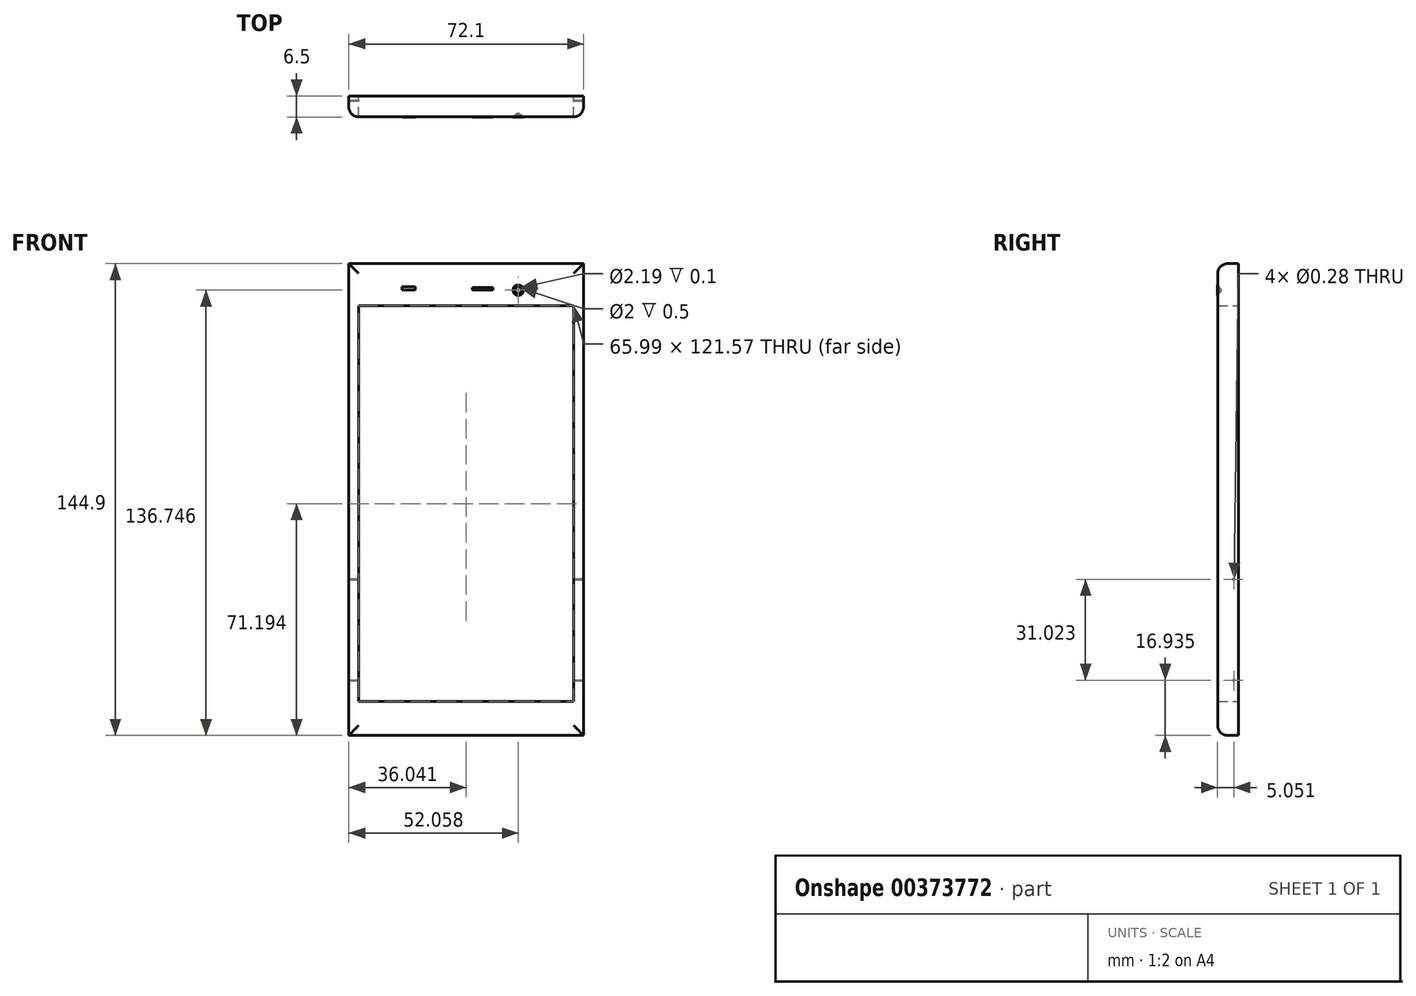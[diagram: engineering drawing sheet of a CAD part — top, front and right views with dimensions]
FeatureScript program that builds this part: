
annotation { "Feature Type Name" : "Feature", "Feature Type Description" : "" }
export const myFeature = defineFeature(function(context is Context, id is Id, definition is map)
    precondition{}
    {
        {
            var Q0;
            Q0=qCreatedBy(makeId("Front.planeOp"),FACE);
            var sketch = newSketch(context, id + "F0", { "sketchPlane" : qUnion([Q0])});
            skLineSegment(sketch, "E0.bottom", {"start": v(-14.1, 97.12) * mm, "end": v(58, 97.12) * mm});
            skLineSegment(sketch, "E0.top", {"start": v(-14.1, -47.78) * mm, "end": v(58, -47.78) * mm});
            skLineSegment(sketch, "E0.left", {"start": v(-14.1, 97.12) * mm, "end": v(-14.1, -47.78) * mm});
            skLineSegment(sketch, "E0.right", {"start": v(58, 97.12) * mm, "end": v(58, -47.78) * mm});
            skLineSegment(sketch, "E1.bottom", {"start": v(-11.05, 84.2) * mm, "end": v(54.93, 84.2) * mm});
            skLineSegment(sketch, "E1.top", {"start": v(-11.05, -37.37) * mm, "end": v(54.93, -37.37) * mm});
            skLineSegment(sketch, "E1.left", {"start": v(-11.05, 84.2) * mm, "end": v(-11.05, -37.37) * mm});
            skLineSegment(sketch, "E1.right", {"start": v(54.93, 84.2) * mm, "end": v(54.93, -37.37) * mm});
            skSolve(sketch);
        }
        {
            var Q0;
            Q0 = qSketchRegion(id + "F0", true);
            extrude(context, id + "F1", {"entities" : qUnion([Q0]), "depth" : 6.4 * mm});
        }
        {
            var Q0;
            Q0=makeQuery(id+"F1.opExtrude","CAP_EDGE",EDGE,{"disambiguationData":[OSD([sQuery(id+"F0.wireOp",EDGE,"E0.bottom")])],"isStart":false});
            var Q1;
            Q1=makeQuery(id+"F1.opExtrude","CAP_EDGE",EDGE,{"disambiguationData":[OSD([sQuery(id+"F0.wireOp",EDGE,"E0.left")])],"isStart":false});
            var Q2;
            Q2=makeQuery(id+"F1.opExtrude","CAP_EDGE",EDGE,{"disambiguationData":[OSD([sQuery(id+"F0.wireOp",EDGE,"E0.top")])],"isStart":false});
            var Q3;
            Q3=makeQuery(id+"F1.opExtrude","CAP_EDGE",EDGE,{"disambiguationData":[OSD([sQuery(id+"F0.wireOp",EDGE,"E0.right")])],"isStart":false});
            fillet(context, id + "F2", {"entities" : qUnion([Q0, Q1, Q2, Q3]), "radius" : 3 * mm, "tangentPropagation" : true, "allowEdgeOverflow" : false});
        }
        {
            var Q0;
            Q0=makeQuery(id+"F1.opExtrude","CAP_FACE",FACE,{"disambiguationData":[OSD([sQuery(id+"F0.wireOp",EDGE,"E0.bottom"),sQuery(id+"F0.wireOp",EDGE,"E0.top"),sQuery(id+"F0.wireOp",EDGE,"E0.left"),sQuery(id+"F0.wireOp",EDGE,"E0.right"),sQuery(id+"F0.wireOp",EDGE,"E1.bottom"),sQuery(id+"F0.wireOp",EDGE,"E1.top"),sQuery(id+"F0.wireOp",EDGE,"E1.left"),sQuery(id+"F0.wireOp",EDGE,"E1.right")])],"isStart":false});
            var sketch = newSketch(context, id + "F3", { "sketchPlane" : qUnion([Q0])});
            skCircle(sketch, "E2", {"center": v(37.96, 88.97) * mm, "radius": 1.62 * mm});
            skLineSegment(sketch, "E3.bottom", {"start": v(23.85, 89.74) * mm, "end": v(30.23, 89.74) * mm});
            skLineSegment(sketch, "E3.top", {"start": v(23.85, 88.97) * mm, "end": v(30.23, 88.97) * mm});
            skLineSegment(sketch, "E3.left", {"start": v(23.85, 89.74) * mm, "end": v(23.85, 88.97) * mm});
            skLineSegment(sketch, "E3.right", {"start": v(30.23, 89.74) * mm, "end": v(30.23, 88.97) * mm});
            skLineSegment(sketch, "E4.bottom", {"start": v(6.36, 88.97) * mm, "end": v(2.2, 88.97) * mm});
            skLineSegment(sketch, "E4.top", {"start": v(6.36, 90.03) * mm, "end": v(2.2, 90.03) * mm});
            skLineSegment(sketch, "E4.left", {"start": v(6.36, 88.97) * mm, "end": v(6.36, 90.03) * mm});
            skLineSegment(sketch, "E4.right", {"start": v(2.2, 88.97) * mm, "end": v(2.2, 90.03) * mm});
            skCircle(sketch, "E5", {"center": v(37.96, 88.97) * mm, "radius": 1.1 * mm});
            skSolve(sketch);
        }
        {
            var Q0;
            Q0 = qSketchRegion(id + "F3", true);
            extrude(context, id + "F4", {"entities" : qUnion([Q0]), "operationType" : NewBodyOperationType.ADD, "endBound" : BoundingType.SYMMETRIC, "oppositeDirection" : true, "depth" : 0.2 * mm});
        }
        {
            var Q0;
            Q0=makeQuery(id+"F1.opExtrude","SWEPT_FACE",FACE,{"disambiguationData":[OSD([sQuery(id+"F0.wireOp",EDGE,"E0.right")])]});
            var sketch = newSketch(context, id + "F5", { "sketchPlane" : qUnion([Q0])});
            skLineSegment(sketch, "E6.bottom", {"start": v(-1.92, -31.47) * mm, "end": v(-1.04, -31.47) * mm});
            skLineSegment(sketch, "E6.top", {"start": v(-1.92, -18.99) * mm, "end": v(-1.04, -18.99) * mm});
            skLineSegment(sketch, "E6.left", {"start": v(-1.92, -31.47) * mm, "end": v(-1.92, -18.99) * mm});
            skLineSegment(sketch, "E6.right", {"start": v(-1.04, -31.47) * mm, "end": v(-1.04, -18.99) * mm});
            skLineSegment(sketch, "E7.bottom", {"start": v(-1.04, -10) * mm, "end": v(-1.87, -10) * mm});
            skLineSegment(sketch, "E7.top", {"start": v(-1.04, 1.2) * mm, "end": v(-1.87, 1.2) * mm});
            skLineSegment(sketch, "E7.left", {"start": v(-1.04, -10) * mm, "end": v(-1.04, 1.2) * mm});
            skLineSegment(sketch, "E7.right", {"start": v(-1.87, -10) * mm, "end": v(-1.87, 1.2) * mm});
            skLineSegment(sketch, "E8.bottom", {"start": v(-1.87, 46) * mm, "end": v(-1.04, 46) * mm});
            skLineSegment(sketch, "E8.top", {"start": v(-1.87, 49.84) * mm, "end": v(-1.04, 49.84) * mm});
            skLineSegment(sketch, "E8.left", {"start": v(-1.87, 46) * mm, "end": v(-1.87, 49.84) * mm});
            skLineSegment(sketch, "E8.right", {"start": v(-1.04, 46) * mm, "end": v(-1.04, 49.84) * mm});
            skLineSegment(sketch, "E9.bottom", {"start": v(-1.04, 59.8) * mm, "end": v(-1.87, 59.8) * mm});
            skLineSegment(sketch, "E9.top", {"start": v(-1.04, 70.8) * mm, "end": v(-1.87, 70.8) * mm});
            skLineSegment(sketch, "E9.left", {"start": v(-1.04, 59.8) * mm, "end": v(-1.04, 70.8) * mm});
            skLineSegment(sketch, "E9.right", {"start": v(-1.87, 59.8) * mm, "end": v(-1.87, 70.8) * mm});
            skCircle(sketch, "E10", {"center": v(-1.45, 0.18) * mm, "radius": 0.16 * mm});
            skCircle(sketch, "E11", {"center": v(-1.45, -30.84) * mm, "radius": 0.18 * mm});
            skSolve(sketch);
        }
        {
            var Q0;
            Q0=sQuery(id+"F5.wireOp",VERTEX,"E11.center");
            var Q1;
            Q1=sQuery(id+"F5.wireOp",VERTEX,"E10.center");
            var Q2;
            Q2=makeQuery(id+"F1.opExtrude","SWEPT_BODY",BODY,{"disambiguationData":[OSD([sQuery(id+"F0.wireOp",EDGE,"E0.bottom"),sQuery(id+"F0.wireOp",EDGE,"E0.top"),sQuery(id+"F0.wireOp",EDGE,"E0.left"),sQuery(id+"F0.wireOp",EDGE,"E0.right"),sQuery(id+"F0.wireOp",EDGE,"E1.bottom"),sQuery(id+"F0.wireOp",EDGE,"E1.top"),sQuery(id+"F0.wireOp",EDGE,"E1.left"),sQuery(id+"F0.wireOp",EDGE,"E1.right")])]});
            hole(context, id + "F6", {"style" : HoleStyle.SIMPLE, "endStyle" : HoleEndStyle.THROUGH, "holeDiameter" : 0.28 * mm, "isTappedThrough" : true, "tappedDepth" : 12 * mm, "tapClearance" : 3, "locations" : qUnion([Q0, Q1]), "scope" : qUnion([Q2])});
        }
        {
            var Q0;
            Q0=sQuery(id+"F5.wireOp",EDGE,"E6.left");
            var Q1;
            Q1=sQuery(id+"F5.wireOp",EDGE,"E6.right");
            var Q2;
            Q2=sQuery(id+"F5.wireOp",EDGE,"E6.bottom");
            var Q3;
            Q3=sQuery(id+"F5.wireOp",EDGE,"E6.top");
            extrude(context, id + "F7", {"bodyType" : ToolBodyType.SURFACE, "surfaceEntities" : qUnion([Q0, Q1, Q2, Q3]), "depth" : 0.1 * mm});
        }
        {
            var Q0;
            Q0=sQuery(id+"F5.wireOp",EDGE,"E7.right");
            var Q1;
            Q1=sQuery(id+"F5.wireOp",EDGE,"E7.left");
            var Q2;
            Q2=sQuery(id+"F5.wireOp",EDGE,"E7.bottom");
            var Q3;
            Q3=sQuery(id+"F5.wireOp",EDGE,"E7.top");
            extrude(context, id + "F8", {"bodyType" : ToolBodyType.SURFACE, "surfaceEntities" : qUnion([Q0, Q1, Q2, Q3]), "depth" : 0.1 * mm});
        }
        {
            var Q0;
            Q0=sQuery(id+"F5.wireOp",EDGE,"E8.left");
            var Q1;
            Q1=sQuery(id+"F5.wireOp",EDGE,"E8.top");
            var Q2;
            Q2=sQuery(id+"F5.wireOp",EDGE,"E8.right");
            var Q3;
            Q3=sQuery(id+"F5.wireOp",EDGE,"E8.bottom");
            extrude(context, id + "F9", {"bodyType" : ToolBodyType.SURFACE, "surfaceEntities" : qUnion([Q0, Q1, Q2, Q3]), "depth" : 0.3 * mm});
        }
        {
            var Q0;
            Q0=sQuery(id+"F5.wireOp",EDGE,"E9.right");
            var Q1;
            Q1=sQuery(id+"F5.wireOp",EDGE,"E9.top");
            var Q2;
            Q2=sQuery(id+"F5.wireOp",EDGE,"E9.left");
            var Q3;
            Q3=sQuery(id+"F5.wireOp",EDGE,"E9.bottom");
            extrude(context, id + "F10", {"bodyType" : ToolBodyType.SURFACE, "surfaceEntities" : qUnion([Q0, Q1, Q2, Q3]), "depth" : 0.3 * mm});
        }
        {
            var Q0;
            Q0=sQuery(id+"F3.wireOp",EDGE,"E4.bottom");
            var Q1;
            Q1=sQuery(id+"F3.wireOp",EDGE,"E4.top");
            var Q2;
            Q2=sQuery(id+"F3.wireOp",EDGE,"E4.left");
            var Q3;
            Q3=sQuery(id+"F3.wireOp",EDGE,"E4.right");
            extrude(context, id + "F11", {"bodyType" : ToolBodyType.SURFACE, "surfaceEntities" : qUnion([Q0, Q1, Q2, Q3]), "oppositeDirection" : true, "depth" : 0.5 * mm});
        }
        {
            var Q0;
            Q0=sQuery(id+"F3.wireOp",EDGE,"E3.bottom");
            var Q1;
            Q1=sQuery(id+"F3.wireOp",EDGE,"E3.top");
            var Q2;
            Q2=sQuery(id+"F3.wireOp",EDGE,"E3.left");
            var Q3;
            Q3=sQuery(id+"F3.wireOp",EDGE,"E3.right");
            extrude(context, id + "F12", {"bodyType" : ToolBodyType.SURFACE, "surfaceEntities" : qUnion([Q0, Q1, Q2, Q3]), "oppositeDirection" : true, "depth" : 0.8 * mm});
        }
        {
            var Q0;
            Q0=sQuery(id+"F3.wireOp",VERTEX,"E2.center");
            var Q1;
            Q1=makeQuery(id+"F1.opExtrude","SWEPT_BODY",BODY,{"disambiguationData":[OSD([sQuery(id+"F0.wireOp",EDGE,"E0.bottom"),sQuery(id+"F0.wireOp",EDGE,"E0.top"),sQuery(id+"F0.wireOp",EDGE,"E0.left"),sQuery(id+"F0.wireOp",EDGE,"E0.right"),sQuery(id+"F0.wireOp",EDGE,"E1.bottom"),sQuery(id+"F0.wireOp",EDGE,"E1.top"),sQuery(id+"F0.wireOp",EDGE,"E1.left"),sQuery(id+"F0.wireOp",EDGE,"E1.right")])]});
            hole(context, id + "F13", {"style" : HoleStyle.SIMPLE, "endStyle" : HoleEndStyle.BLIND, "holeDiameter" : 2 * mm, "holeDepth" : 0.5 * mm, "isTappedThrough" : true, "tappedDepth" : 12 * mm, "tapClearance" : 3, "locations" : qUnion([Q0]), "scope" : qUnion([Q1])});
        }
    });
